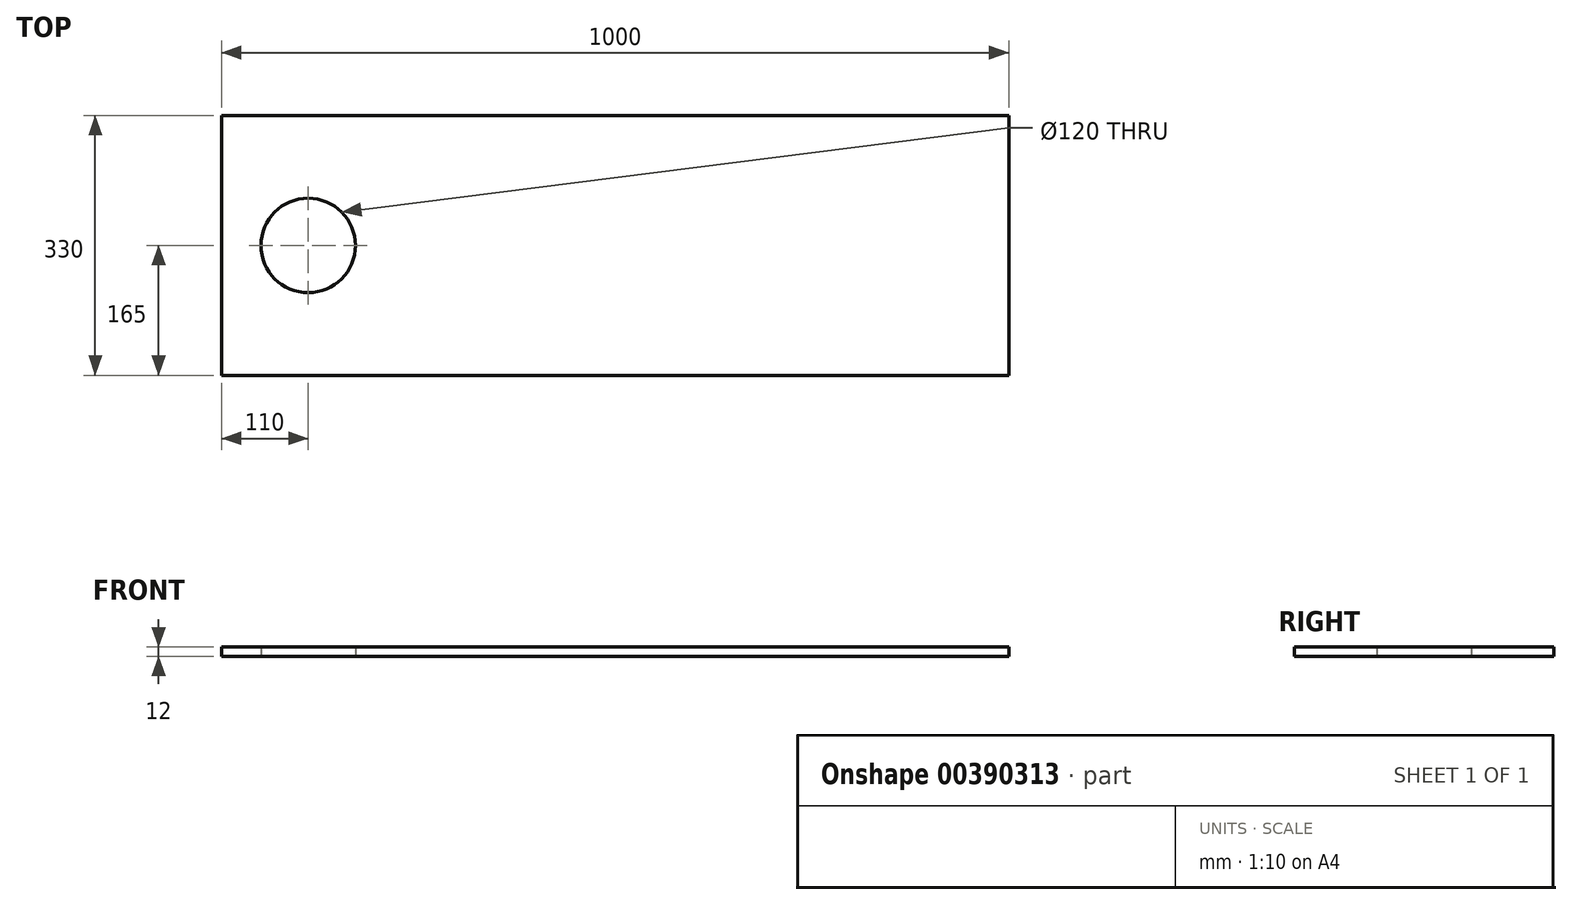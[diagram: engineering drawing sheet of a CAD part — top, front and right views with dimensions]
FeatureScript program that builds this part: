
annotation { "Feature Type Name" : "Feature", "Feature Type Description" : "" }
export const myFeature = defineFeature(function(context is Context, id is Id, definition is map)
    precondition{}
    {
        {
            var Q0;
            Q0=qCreatedBy(makeId("Top.planeOp"),FACE);
            var sketch = newSketch(context, id + "F0", { "sketchPlane" : qUnion([Q0])});
            skLineSegment(sketch, "E0.bottom", {"start": v(0, 0) * mm, "end": v(1000, 0) * mm});
            skLineSegment(sketch, "E0.top", {"start": v(0, 330) * mm, "end": v(1000, 330) * mm});
            skLineSegment(sketch, "E0.left", {"start": v(0, 0) * mm, "end": v(0, 330) * mm});
            skLineSegment(sketch, "E0.right", {"start": v(1000, 0) * mm, "end": v(1000, 330) * mm});
            skCircle(sketch, "E1", {"center": v(110, 165) * mm, "radius": 60 * mm});
            skSolve(sketch);
        }
        {
            var Q0;
            Q0=makeQuery(id+"F0.imprint","IMPRINT",FACE,{"disambiguationData":[TD([[makeQuery(id+"F0.imprint","IMPRINT",EDGE,{"derivedFrom":sQuery(id+"F0.wireOp",EDGE,"E0.bottom")}),1.0]])]});
            extrude(context, id + "F1", {"entities" : qUnion([Q0]), "depth" : 12 * mm});
        }
    });
